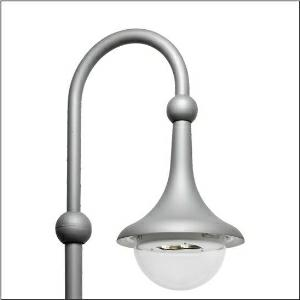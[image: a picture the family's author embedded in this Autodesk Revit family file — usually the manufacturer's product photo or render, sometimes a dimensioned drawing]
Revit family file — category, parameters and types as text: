
# Revit family: grosse_glocke_iq___st1_2a_5xa1565a1f108_90a8
name_source: partatom
category: Lighting Fixtures
units: mm (PartAtom-declared; Revit-internal decimal feet)

## family parameters
Cut with Voids When Loaded = No
Host = Face
Light Source = No
Part Type = Normal
Room Calculation Point = No
Round Connector Dimension = Use Diameter
Shared = No

## types (1)
- --- (1 x LED, 4180 lm, 34.3 W, 2200K)
    Apparent Load = 34 VA
    CIE Flux Codes = 28 66 95 100 100
    Color Rendering = 70
    Color Temperature = 2200K
    Default Elevation = 1800 mm
    Description = Large Bell iQ, mast luminaire, primary light control with 3 zone facetted reflector, of plastic, silver coated, primary optical cover: enclosure, of PMMA, transparent, light distribution: ST1.2a, light emission: direct distribution, primary light characteristic: asymmetric, installation type: suspended mounting, High Power LED, rated luminous flux: 4.180lm, luminous efficacy: 122lm/W, light colour: 722, colour temperature: 2200K, control gear: iQ Street-Remote, control: optimised constant luminous flux control (CLO 2.0), Desk-Remote (wireless, voltage-free reading and setting of iQ features in the workshop via application-optimized NFC function/RFID function), Light-Fading, Smart-Wire, Night-Set, Lumen-Switch, Temp-Guard, Auto-Match, Street-Remote, pre-setting: logarithmic dimming characteristic, mains connection: 230..240V, AC, 50/60Hz, start of lifetime: 34W, end of service life: 38W, reduction: 16W, luminaire housing, bell-shaped, of glass-fibre reinforced polyester, coated, Siteco® metallic grey (DB 702S), please order curved mast extension separately, diameter: 530mm, height: 695mm, mounting height: 4..6m, protection rating (complete): IP54, insulation class (complete): insulation class II (safety insulation), certification: CE, ENEC, VDE, impact resistance: IK08, standard-compliant lighting for roads and squares, packaging unit: 1 piece

Light Distribution: ST1.2a
    Height = 695 mm
    Lamp = 1 x LED
    Lamp Light Flux = 4180 lm
    Lamp Power = 34.3 W
    Lamp count = 1
    Length = 530 mm
    Luminous efficacy = 122 lm/W
    Manufacturer = Siteco
    ModVariant = No
    Model = 5XA1565A1F108
    Number of Poles = 1
    OnlyDefault = Yes
    Power Factor = 1
    Product Name = Große Glocke iQ | ST1.2a
    Product group = mast luminaire | pylon annexe
    ProductGroupID = 6200
    Protection Class = Protection class II
    Protection Degree = IP 54
    RLX_Detail_Level = 1
    RLX_Emergency_Light_Flux = 0 lm
    RLX_Emergency_Type = 0
    RLX_Emergency_Type_DB = No
    RlxData = <blob elided: 71649 chars, md5=de727eec>
    Socket = socket
    Standby Power = 0 W
    System Light Flux = 4180 lm
    System Power = 34 W
    Type Comments = factory setting: luminous flux: 100 % | dim-lin: 254 | 640 mA
    Type Image = l_1347688.jpg
    URL = http://relux.com
    VarID = @adj_080019
    Voltage = 0 V
    Weight = 0.00 kg
    Width = 0 mm  [stored 0 ft]

note: [stored X ft] marks values corroborated as IEEE doubles in the binary element streams (Revit-internal decimal feet)

## geometry (parser evidence)
native form markers: Blend x4, Sweep x11
no freeform markers — native parametric forms only
